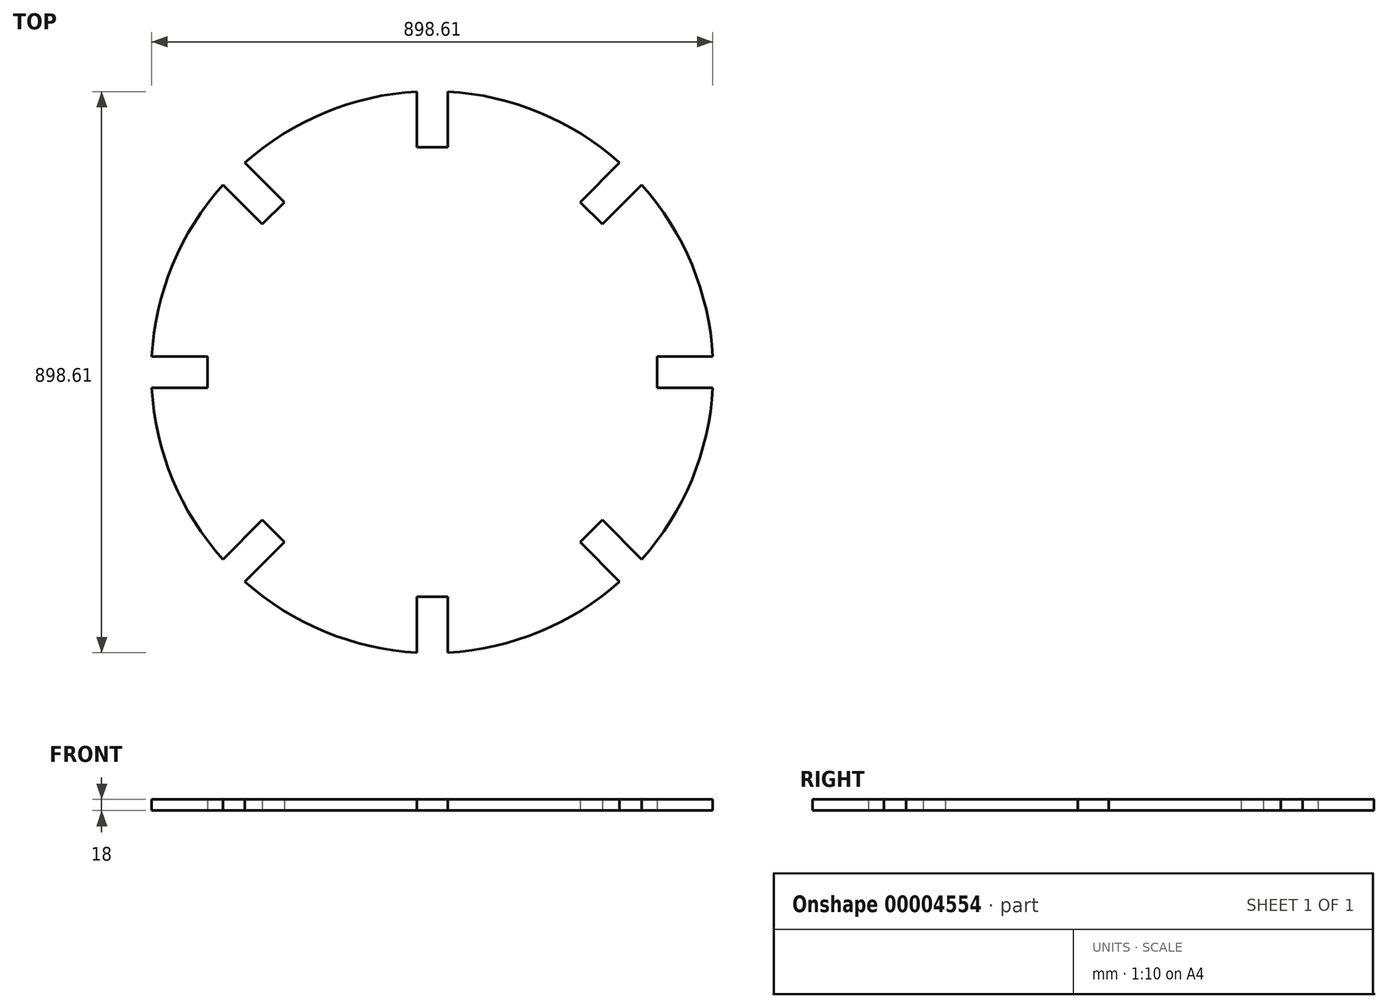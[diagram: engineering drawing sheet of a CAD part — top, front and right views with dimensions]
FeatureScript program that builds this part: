
annotation { "Feature Type Name" : "Feature", "Feature Type Description" : "" }
export const myFeature = defineFeature(function(context is Context, id is Id, definition is map)
    precondition{}
    {
        {
            var Q0;
            Q0=qCreatedBy(makeId("Top.planeOp"),FACE);
            var sketch = newSketch(context, id + "F0", { "sketchPlane" : qUnion([Q0])});
            skCircle(sketch, "E0", {"center": v(-365.51, 95.4) * mm, "radius": 450 * mm});
            skLineSegment(sketch, "E1", {"start": v(-365.51, 95.4) * mm, "end": v(-365.51, -743.08) * mm, "construction": true});
            skLineSegment(sketch, "E2.rect.bottom", {"start": v(-340.51, -264.6) * mm, "end": v(-390.51, -264.6) * mm});
            skLineSegment(sketch, "E2.rect.top", {"start": v(-340.51, -383.08) * mm, "end": v(-390.51, -383.08) * mm});
            skLineSegment(sketch, "E2.rect.left", {"start": v(-340.51, -264.6) * mm, "end": v(-340.51, -383.08) * mm});
            skLineSegment(sketch, "E2.rect.right", {"start": v(-390.51, -264.6) * mm, "end": v(-390.51, -383.08) * mm});
            skPoint(sketch, "E2.rect.middle", {"position": v(-365.51, -323.84) * mm});
            skSolve(sketch);
        }
        {
            var Q0;
            {var subQ3=sQuery(id+"F0.wireOp",EDGE,"E2.rect.bottom");Q0=makeQuery(id+"F0.imprint","IMPRINT",FACE,{"disambiguationData":[TD([[makeQuery(id+"F0.imprint","IMPRINT",EDGE,{"derivedFrom":subQ3}),1.0]])]});}
            var Q1;
            {var subQ3=sQuery(id+"F0.wireOp",EDGE,"E2.rect.bottom");Q1=makeQuery(id+"F0.imprint","IMPRINT",FACE,{"disambiguationData":[TD([[makeQuery(id+"F0.imprint","IMPRINT",EDGE,{"derivedFrom":subQ3}),-1.0]])]});}
            extrude(context, id + "F1", {"entities" : qUnion([Q0, Q1]), "depth" : 18 * mm});
        }
        {
            var Q0;
            {var subQ3=sQuery(id+"F0.wireOp",EDGE,"E2.rect.bottom");Q0=makeQuery(id+"F0.imprint","IMPRINT",FACE,{"disambiguationData":[TD([[makeQuery(id+"F0.imprint","IMPRINT",EDGE,{"derivedFrom":subQ3}),1.0]])]});}
            extrude(context, id + "F2", {"entities" : qUnion([Q0]), "operationType" : NewBodyOperationType.REMOVE, "endBound" : BoundingType.UP_TO_NEXT, "depth" : 25 * mm});
        }
        {
            var Q0;
            Q0=makeQuery(id+"F2.boolean.opBoolean","COPY",FACE,{"derivedFrom":makeQuery(id+"F2.opExtrude","SWEPT_FACE",FACE,{"disambiguationData":[OSD([sQuery(id+"F0.wireOp",EDGE,"E2.rect.left")])]})});
            var Q1;
            Q1=makeQuery(id+"F2.boolean.opBoolean","COPY",FACE,{"derivedFrom":makeQuery(id+"F2.opExtrude","SWEPT_FACE",FACE,{"disambiguationData":[OSD([sQuery(id+"F0.wireOp",EDGE,"E2.rect.bottom")])]})});
            var Q2;
            Q2=makeQuery(id+"F2.boolean.opBoolean","COPY",FACE,{"derivedFrom":makeQuery(id+"F2.opExtrude","SWEPT_FACE",FACE,{"disambiguationData":[OSD([sQuery(id+"F0.wireOp",EDGE,"E2.rect.right")])]})});
            var Q3;
            Q3=makeQuery(id+"F1.opExtrude","SWEPT_BODY",BODY,{"disambiguationData":[OSD([sQuery(id+"F0.wireOp",EDGE,"E0")])]});
            var Q4;
            Q4=makeQuery(id+"F1.opExtrude","CAP_EDGE",EDGE,{"disambiguationData":[OSD([sQuery(id+"F0.wireOp",EDGE,"E0")])],"isStart":false});
            circularPattern(context, id + "F3", {"faces" : qUnion([Q0, Q1, Q2]), "axis" : qUnion([Q4]), "angle" : 360 * degree, "instanceCount" : 8, "equalSpace" : true, "patternType" : PatternType.FACE});
        }
        {
            var Q0;
            Q0=qCreatedBy(makeId("Front.planeOp"),FACE);
            var sketch = newSketch(context, id + "F4", { "sketchPlane" : qUnion([Q0])});
            skLineSegment(sketch, "E3", {"start": v(355.7, 350.59) * mm, "end": v(355.7, -41.28) * mm, "construction": true});
            skLineSegment(sketch, "E4", {"start": v(355.7, -41.28) * mm, "end": v(1355.7, -41.28) * mm});
            skLineSegment(sketch, "E5", {"start": v(1355.7, -41.28) * mm, "end": v(1355.7, 69.96) * mm});
            skLineSegment(sketch, "E6", {"start": v(1355.7, 69.96) * mm, "end": v(398.4, 308.72) * mm});
            skLineSegment(sketch, "E7.0.MirrorCS", {"start": v(-644.3, 69.96) * mm, "end": v(313, 308.72) * mm});
            skLineSegment(sketch, "E8.0.MirrorCS", {"start": v(-644.3, -41.28) * mm, "end": v(-644.3, 69.96) * mm});
            skLineSegment(sketch, "E9.0.MirrorCS", {"start": v(355.7, -41.28) * mm, "end": v(-644.3, -41.28) * mm});
            skLineSegment(sketch, "E10.0.MirrorCS", {"start": v(313, 308.72) * mm, "end": v(313, 133.72) * mm});
            skLineSegment(sketch, "E11", {"start": v(330.7, 308.72) * mm, "end": v(330.7, 133.72) * mm});
            skLineSegment(sketch, "E12", {"start": v(330.7, 133.72) * mm, "end": v(313, 133.72) * mm});
            skLineSegment(sketch, "E13", {"start": v(330.7, 308.72) * mm, "end": v(355.7, 308.72) * mm});
            skLineSegment(sketch, "E14.0.MirrorCS", {"start": v(380.7, 308.72) * mm, "end": v(380.7, 133.72) * mm});
            skLineSegment(sketch, "E14.1.MirrorCS", {"start": v(398.4, 308.72) * mm, "end": v(398.4, 133.72) * mm});
            skLineSegment(sketch, "E14.2.MirrorCS", {"start": v(380.7, 133.72) * mm, "end": v(398.4, 133.72) * mm});
            skLineSegment(sketch, "E14.3.MirrorCS", {"start": v(380.7, 308.72) * mm, "end": v(355.7, 308.72) * mm});
            skSolve(sketch);
        }
        {
            var Q0;
            Q0=qSketchRegion(id+"F4",true);
            extrude(context, id + "F5", {"entities" : qUnion([Q0]), "depth" : 18 * mm});
        }
        {
            var Q0;
            Q0=qCreatedBy(makeId("Front.planeOp"),FACE);
            var sketch = newSketch(context, id + "F6", { "sketchPlane" : qUnion([Q0])});
            skLineSegment(sketch, "E15", {"start": v(1876.04, 0) * mm, "end": v(2866.04, 0) * mm});
            skLineSegment(sketch, "E16", {"start": v(2866.04, 0) * mm, "end": v(2866.04, 110.73) * mm});
            skLineSegment(sketch, "E17", {"start": v(2866.04, 110.73) * mm, "end": v(1866.04, 350) * mm});
            skLineSegment(sketch, "E18", {"start": v(1866.04, 350) * mm, "end": v(1866.04, 0) * mm, "construction": true});
            skLineSegment(sketch, "E19", {"start": v(1866.04, 175) * mm, "end": v(1876.04, 175) * mm});
            skLineSegment(sketch, "E20", {"start": v(1876.04, 175) * mm, "end": v(1876.04, 0) * mm});
            skLineSegment(sketch, "E21.0.MirrorCS", {"start": v(866.04, 110.73) * mm, "end": v(1866.04, 350) * mm});
            skLineSegment(sketch, "E22.0.MirrorCS", {"start": v(866.04, 0) * mm, "end": v(866.04, 110.73) * mm});
            skLineSegment(sketch, "E23.0.MirrorCS", {"start": v(1856.04, 0) * mm, "end": v(866.04, 0) * mm});
            skLineSegment(sketch, "E24.0.MirrorCS", {"start": v(1856.04, 175) * mm, "end": v(1856.04, 0) * mm});
            skLineSegment(sketch, "E25.0.MirrorCS", {"start": v(1866.04, 175) * mm, "end": v(1856.04, 175) * mm});
            skSolve(sketch);
        }
        {
            var Q0;
            Q0=qSketchRegion(id+"F6",true);
            extrude(context, id + "F7", {"entities" : qUnion([Q0]), "depth" : 18 * mm});
        }
        {
            var Q0;
            Q0=makeQuery(id+"F7.opExtrude","SWEPT_BODY",BODY,{"disambiguationData":[OSD([sQuery(id+"F6.wireOp",EDGE,"E15"),sQuery(id+"F6.wireOp",EDGE,"E16"),sQuery(id+"F6.wireOp",EDGE,"E17"),sQuery(id+"F6.wireOp",EDGE,"E20"),sQuery(id+"F6.wireOp",EDGE,"E21.0.MirrorCS"),sQuery(id+"F6.wireOp",EDGE,"E22.0.MirrorCS"),sQuery(id+"F6.wireOp",EDGE,"E23.0.MirrorCS"),sQuery(id+"F6.wireOp",EDGE,"E24.0.MirrorCS"),sQuery(id+"F6.wireOp",EDGE,"E25.0.MirrorCS")])]});
            deleteBodies(context, id + "F8", {"entities" : qUnion([Q0])});
        }
        {
            var Q0;
            Q0=makeQuery(id+"F5.opExtrude","SWEPT_BODY",BODY,{"disambiguationData":[OSD([sQuery(id+"F4.wireOp",EDGE,"E5"),sQuery(id+"F4.wireOp",EDGE,"E6"),sQuery(id+"F4.wireOp",EDGE,"E7.0.MirrorCS"),sQuery(id+"F4.wireOp",EDGE,"E8.0.MirrorCS"),sQuery(id+"F4.wireOp",EDGE,"E9.0.MirrorCS"),sQuery(id+"F4.wireOp",EDGE,"E10.0.MirrorCS"),sQuery(id+"F4.wireOp",EDGE,"E11"),sQuery(id+"F4.wireOp",EDGE,"E12"),sQuery(id+"F4.wireOp",EDGE,"E14.0.MirrorCS"),sQuery(id+"F4.wireOp",EDGE,"E14.1.MirrorCS"),sQuery(id+"F4.wireOp",EDGE,"E14.2.MirrorCS"),sQuery(id+"F4.wireOp",EDGE,"E14.3.MirrorCS")])]});
            deleteBodies(context, id + "F9", {"entities" : qUnion([Q0])});
        }
    });
